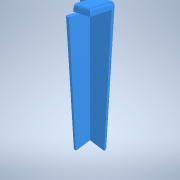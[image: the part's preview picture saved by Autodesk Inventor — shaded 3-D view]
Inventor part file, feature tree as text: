
AUTODESK INVENTOR PART (.ipt)
format: ipt  version: 2021 (Build 250183000, 183)  size: 160,768 bytes
history: native  units: mm
features: extrude x5, sketch x4, fillet x1
ambient origin geometry x8: Origin, YZ Plane, XZ Plane, XY Plane, X Axis, Y Axis, Z Axis, Center Point
bodies: Solid1 (feature_tree)
feature tree (10):
  extrude  "Extrusion1"  Depth=15.0mm
  extrude  "Extrusion3"  Depth=3.0mm
  extrude  "Extrusion4"  Depth=12.0mm
  fillet  "Fillet3"  Radius=3.0mm
  extrude  "Extrusion7"  Depth=12.0mm TaperAngle=0.0deg
  extrude  "Extrusion8"  Depth=2.0mm
  sketch  "Sketch4"  dims[d0=15.0mm d1=15.0mm]
  sketch  "Sketch6"  dims[d2=86.0mm d3=0.0mm d10=3.0mm]
  sketch  "Sketch11"  dims[d11=12.0mm d12=12.0mm d13=3.0mm]
  sketch  "Sketch12"  dims[d14=3.0mm d15=0.0mm d16=12.0mm d17=0.0mm d18=2.0mm d31=6.0mm d32=0.0mm d46=0.0mm d47=0.0mm]
